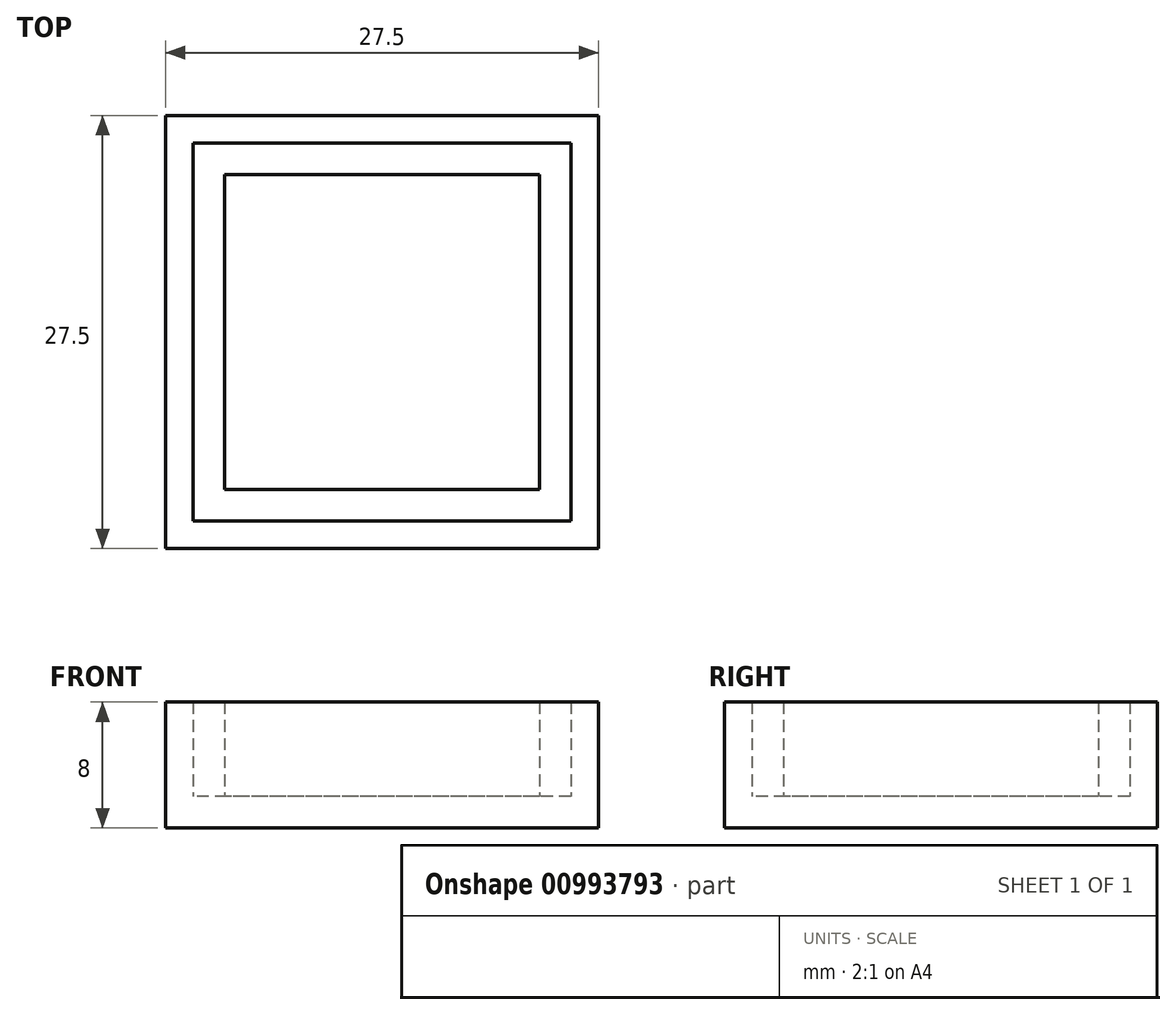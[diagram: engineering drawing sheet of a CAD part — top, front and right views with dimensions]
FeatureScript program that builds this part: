
annotation { "Feature Type Name" : "Feature", "Feature Type Description" : "" }
export const myFeature = defineFeature(function(context is Context, id is Id, definition is map)
    precondition{}
    {
        {
            var Q0;
            Q0=qCreatedBy(makeId("Top.planeOp"),FACE);
            var sketch = newSketch(context, id + "F0", { "sketchPlane" : qUnion([Q0])});
            skLineSegment(sketch, "E0.bottom", {"start": v(13.75, 13.75) * mm, "end": v(-13.75, 13.75) * mm});
            skLineSegment(sketch, "E0.top", {"start": v(13.75, -13.75) * mm, "end": v(-13.75, -13.75) * mm});
            skLineSegment(sketch, "E0.left", {"start": v(13.75, 13.75) * mm, "end": v(13.75, -13.75) * mm});
            skLineSegment(sketch, "E0.right", {"start": v(-13.75, 13.75) * mm, "end": v(-13.75, -13.75) * mm});
            skPoint(sketch, "E0.middle", {"position": v(0, 0) * mm});
            skLineSegment(sketch, "E1.bottom", {"start": v(12, 12) * mm, "end": v(-12, 12) * mm});
            skLineSegment(sketch, "E1.top", {"start": v(12, -12) * mm, "end": v(-12, -12) * mm});
            skLineSegment(sketch, "E1.left", {"start": v(12, 12) * mm, "end": v(12, -12) * mm});
            skLineSegment(sketch, "E1.right", {"start": v(-12, 12) * mm, "end": v(-12, -12) * mm});
            skLineSegment(sketch, "E2.0", {"start": v(-10, 10) * mm, "end": v(-10, -10) * mm});
            skLineSegment(sketch, "E2.1", {"start": v(10, 10) * mm, "end": v(-10, 10) * mm});
            skLineSegment(sketch, "E2.2", {"start": v(10, 10) * mm, "end": v(10, -10) * mm});
            skLineSegment(sketch, "E2.3", {"start": v(10, -10) * mm, "end": v(-10, -10) * mm});
            skSolve(sketch);
        }
        {
            var Q0;
            Q0=makeQuery(id+"F0.imprint","IMPRINT",FACE,{"disambiguationData":[TD([[makeQuery(id+"F0.imprint","IMPRINT",EDGE,{"derivedFrom":sQuery(id+"F0.wireOp",EDGE,"E2.0")}),1.0]])]});
            var Q1;
            Q1=makeQuery(id+"F0.imprint","IMPRINT",FACE,{"disambiguationData":[TD([[makeQuery(id+"F0.imprint","IMPRINT",EDGE,{"derivedFrom":sQuery(id+"F0.wireOp",EDGE,"E1.bottom")}),1.0]])]});
            var Q2;
            Q2=makeQuery(id+"F0.imprint","IMPRINT",FACE,{"disambiguationData":[TD([[makeQuery(id+"F0.imprint","IMPRINT",EDGE,{"derivedFrom":sQuery(id+"F0.wireOp",EDGE,"E0.bottom")}),1.0]])]});
            extrude(context, id + "F1", {"entities" : qUnion([Q0, Q1, Q2]), "oppositeDirection" : true, "depth" : 2 * mm, "offsetDistance" : 25 * mm});
        }
        {
            var Q0;
            Q0=makeQuery(id+"F0.imprint","IMPRINT",FACE,{"disambiguationData":[TD([[makeQuery(id+"F0.imprint","IMPRINT",EDGE,{"derivedFrom":sQuery(id+"F0.wireOp",EDGE,"E2.0")}),1.0]])]});
            var Q1;
            Q1=makeQuery(id+"F0.imprint","IMPRINT",FACE,{"disambiguationData":[TD([[makeQuery(id+"F0.imprint","IMPRINT",EDGE,{"derivedFrom":sQuery(id+"F0.wireOp",EDGE,"E0.bottom")}),1.0]])]});
            extrude(context, id + "F2", {"entities" : qUnion([Q0, Q1]), "operationType" : NewBodyOperationType.ADD, "depth" : 6 * mm, "offsetDistance" : 25 * mm});
        }
    });
